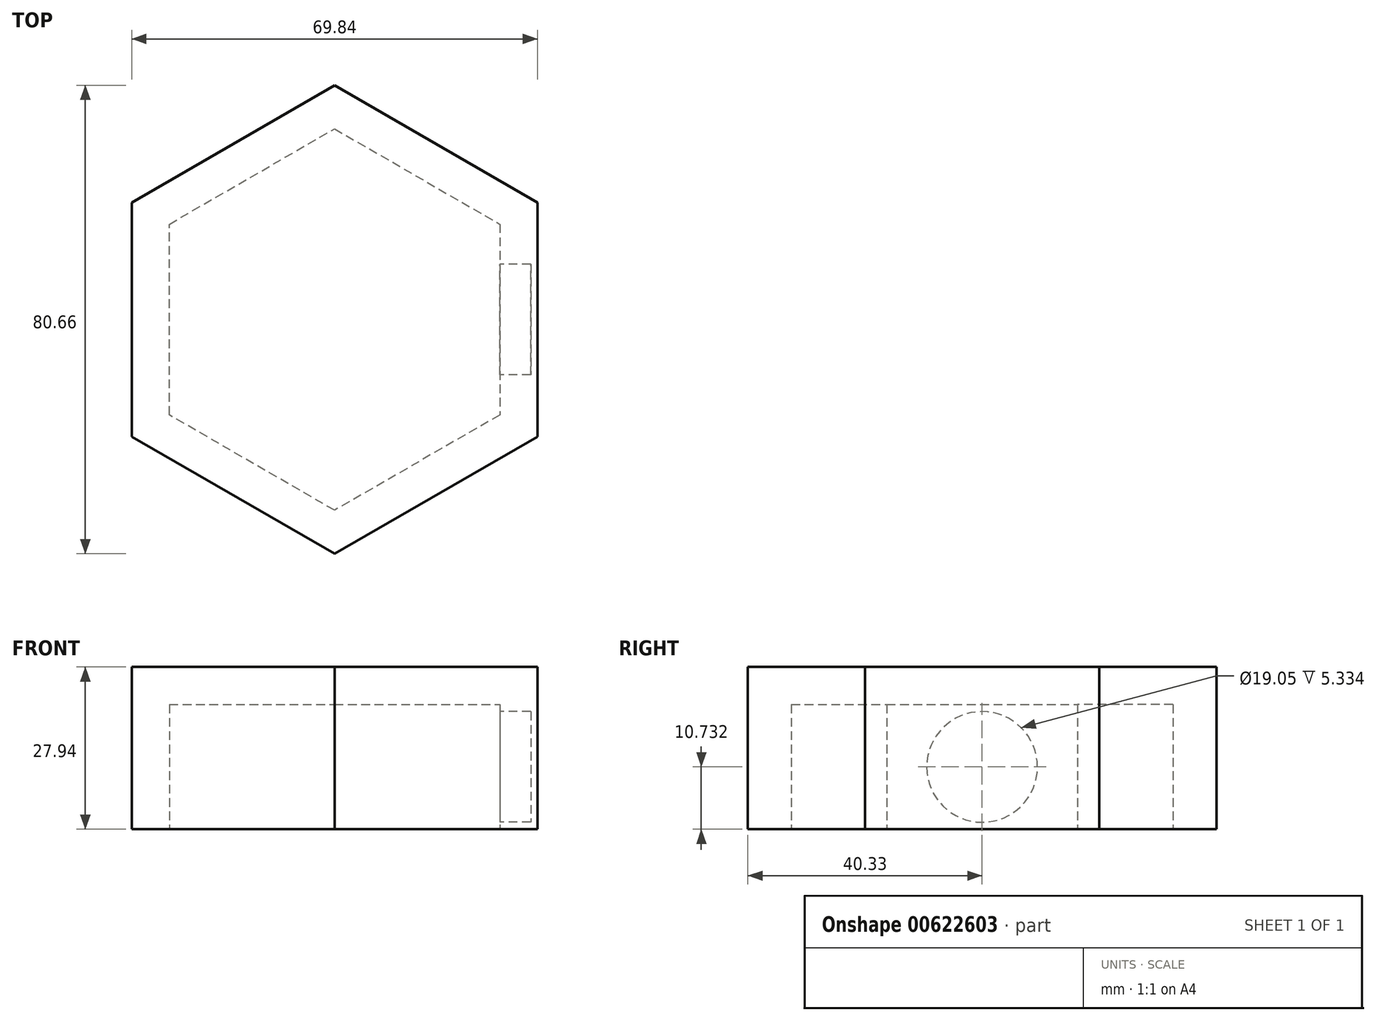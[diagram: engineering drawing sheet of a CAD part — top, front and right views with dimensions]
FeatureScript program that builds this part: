
annotation { "Feature Type Name" : "Feature", "Feature Type Description" : "" }
export const myFeature = defineFeature(function(context is Context, id is Id, definition is map)
    precondition{}
    {
        {
            var Q0;
            Q0=qCreatedBy(makeId("Top.planeOp"),FACE);
            var sketch = newSketch(context, id + "F0", { "sketchPlane" : qUnion([Q0])});
            skCircle(sketch, "E0.cCircle", {"center": v(0, 0) * mm, "radius": 34.93 * mm, "construction": true});
            skLineSegment(sketch, "E0.0", {"start": v(0, 40.33) * mm, "end": v(34.93, 20.16) * mm});
            skLineSegment(sketch, "E0.1", {"start": v(34.92, 20.16) * mm, "end": v(34.93, -20.16) * mm});
            skLineSegment(sketch, "E0.2", {"start": v(34.93, -20.16) * mm, "end": v(0, -40.33) * mm});
            skLineSegment(sketch, "E0.3", {"start": v(0, -40.33) * mm, "end": v(-34.92, -20.16) * mm});
            skLineSegment(sketch, "E0.4", {"start": v(-34.92, -20.16) * mm, "end": v(-34.93, 20.16) * mm});
            skLineSegment(sketch, "E0.5", {"start": v(-34.93, 20.16) * mm, "end": v(0, 40.33) * mm});
            skPoint(sketch, "E0.0.midPoint", {"position": v(17.46, 30.25) * mm});
            skSolve(sketch);
        }
        {
            var Q0;
            Q0 = qSketchRegion(id + "F0", true);
            extrude(context, id + "F1", {"entities" : qUnion([Q0]), "depth" : 27.94 * mm, "offsetDistance" : 25.4 * mm});
        }
        {
            var Q0;
            Q0=makeQuery(id+"F1.opExtrude","CAP_FACE",FACE,{"disambiguationData":[OSD([sQuery(id+"F0.wireOp",EDGE,"E0.0"),sQuery(id+"F0.wireOp",EDGE,"E0.1"),sQuery(id+"F0.wireOp",EDGE,"E0.2"),sQuery(id+"F0.wireOp",EDGE,"E0.3"),sQuery(id+"F0.wireOp",EDGE,"E0.4"),sQuery(id+"F0.wireOp",EDGE,"E0.5")])],"isStart":true});
            shell(context, id + "F2", {"entities" : qUnion([Q0]), "thickness" : 6.48 * mm});
        }
        {
            var Q0;
            Q0=makeQuery(id+"F2.opShell","OFFSET_FACE",FACE,{"disambiguationData":[OSD([sQuery(id+"F0.wireOp",EDGE,"E0.1")])]});
            var sketch = newSketch(context, id + "F3", { "sketchPlane" : qUnion([Q0])});
            skCircle(sketch, "E1", {"center": v(0, 10.73) * mm, "radius": 9.53 * mm});
            skPoint(sketch, "E1.centerSnap0", {"position": v(-16.42, 10.73) * mm});
            skSolve(sketch);
        }
        {
            var Q0;
            Q0=makeQuery(id+"F3.imprint","IMPRINT",FACE,{"disambiguationData":[TD([[makeQuery(id+"F3.imprint","IMPRINT",EDGE,{"derivedFrom":sQuery(id+"F3.wireOp",EDGE,"E1")}),1.0]])]});
            extrude(context, id + "F4", {"entities" : qUnion([Q0]), "operationType" : NewBodyOperationType.REMOVE, "oppositeDirection" : true, "depth" : 5.33 * mm, "offsetDistance" : 25.4 * mm});
        }
    });
